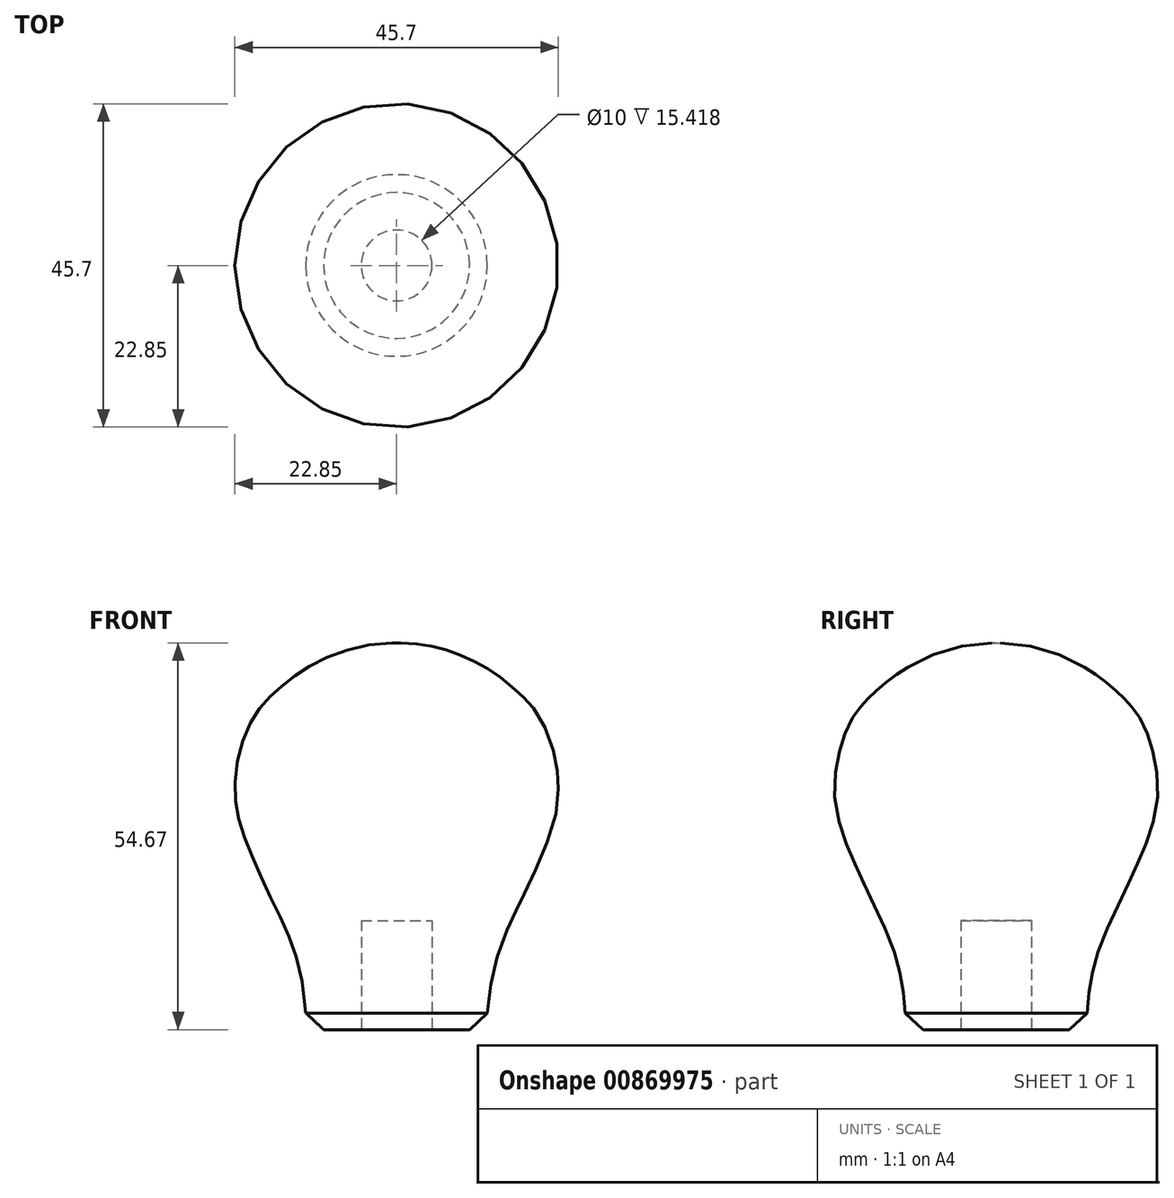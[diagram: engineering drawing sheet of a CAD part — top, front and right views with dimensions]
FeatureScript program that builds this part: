
annotation { "Feature Type Name" : "Feature", "Feature Type Description" : "" }
export const myFeature = defineFeature(function(context is Context, id is Id, definition is map)
    precondition{}
    {
        {
            var Q0;
            Q0=qCreatedBy(makeId("Front.planeOp"),FACE);
            var sketch = newSketch(context, id + "F0", { "sketchPlane" : qUnion([Q0])});
            skLineSegment(sketch, "E0", {"start": v(0, 110.67) * mm, "end": v(0, -110.4) * mm});
            skFitSpline(sketch, "E1", {"points": [v(0, -16.38) * mm, v(-11.02, -19) * mm, v(-16.69, -22.9) * mm, v(-20.66, -27.64) * mm, v(-22.85, -36.87) * mm, v(-21.07, -45.02) * mm, v(-16.28, -55.53) * mm, v(-12.7, -71.04) * mm], "startDerivative": vector(-78.86, 2.75) * mm, "endDerivative": vector(5.91, -137.64) * mm});
            skLineSegment(sketch, "E2", {"start": v(-12.7, -71.04) * mm, "end": v(0, -71.04) * mm});
            skLineSegment(sketch, "E3.bottom", {"start": v(-25.4, -13.27) * mm, "end": v(0, -13.27) * mm});
            skLineSegment(sketch, "E3.top", {"start": v(-25.4, -76.77) * mm, "end": v(0, -76.77) * mm});
            skLineSegment(sketch, "E3.left", {"start": v(-25.4, -13.27) * mm, "end": v(-25.4, -76.77) * mm});
            skLineSegment(sketch, "E3.right", {"start": v(0, -13.27) * mm, "end": v(0, -76.77) * mm});
            skPoint(sketch, "E4", {"position": v(-25.4, -45.02) * mm});
            skCircle(sketch, "E5", {"center": v(0, -40.98) * mm, "radius": 24.6 * mm, "construction": true});
            skSolve(sketch);
        }
        {
            var Q0;
            {var subQ0=sQuery(id+"F0.wireOp",EDGE,"E1");Q0=makeQuery(id+"F0.imprint","IMPRINT",FACE,{"disambiguationData":[TD([[makeQuery(id+"F0.imprint","IMPRINT",EDGE,{"derivedFrom":subQ0}),1.0]])]});}
            var Q1;
            Q1=sQuery(id+"F0.wireOp",EDGE,"E0");
            revolve(context, id + "F1", {"surfaceOperationType" : NewSurfaceOperationType.NEW, "entities" : qUnion([Q0]), "axis" : qUnion([Q1]), "revolveType" : RevolveType.FULL});
        }
        {
            var Q0;
            Q0=makeQuery(id+"F1.opRevolve","SWEPT_EDGE",EDGE,{"disambiguationData":[OSD([sQuery(id+"F0.wireOp",EDGE,"E1"),sQuery(id+"F0.wireOp",EDGE,"E2")])]});
            chamfer(context, id + "F2", {"entities" : qUnion([Q0]), "width" : 2.54 * mm, "tangentPropagation" : true});
        }
        {
            var Q0;
            Q0=makeQuery(id+"F1.opRevolve","SWEPT_FACE",FACE,{"disambiguationData":[OSD([sQuery(id+"F0.wireOp",EDGE,"E2")])]});
            var sketch = newSketch(context, id + "F3", { "sketchPlane" : qUnion([Q0])});
            skCircle(sketch, "E6", {"center": v(0, 0) * mm, "radius": 5 * mm});
            skSolve(sketch);
        }
        {
            var Q0;
            Q0=makeQuery(id+"F3.imprint","IMPRINT",FACE,{"disambiguationData":[TD([[makeQuery(id+"F3.imprint","IMPRINT",EDGE,{"derivedFrom":sQuery(id+"F3.wireOp",EDGE,"E6")}),1.0]])]});
            extrude(context, id + "F4", {"entities" : qUnion([Q0]), "operationType" : NewBodyOperationType.REMOVE, "oppositeDirection" : true, "depth" : 15.42 * mm, "offsetDistance" : 25.4 * mm});
        }
    });
